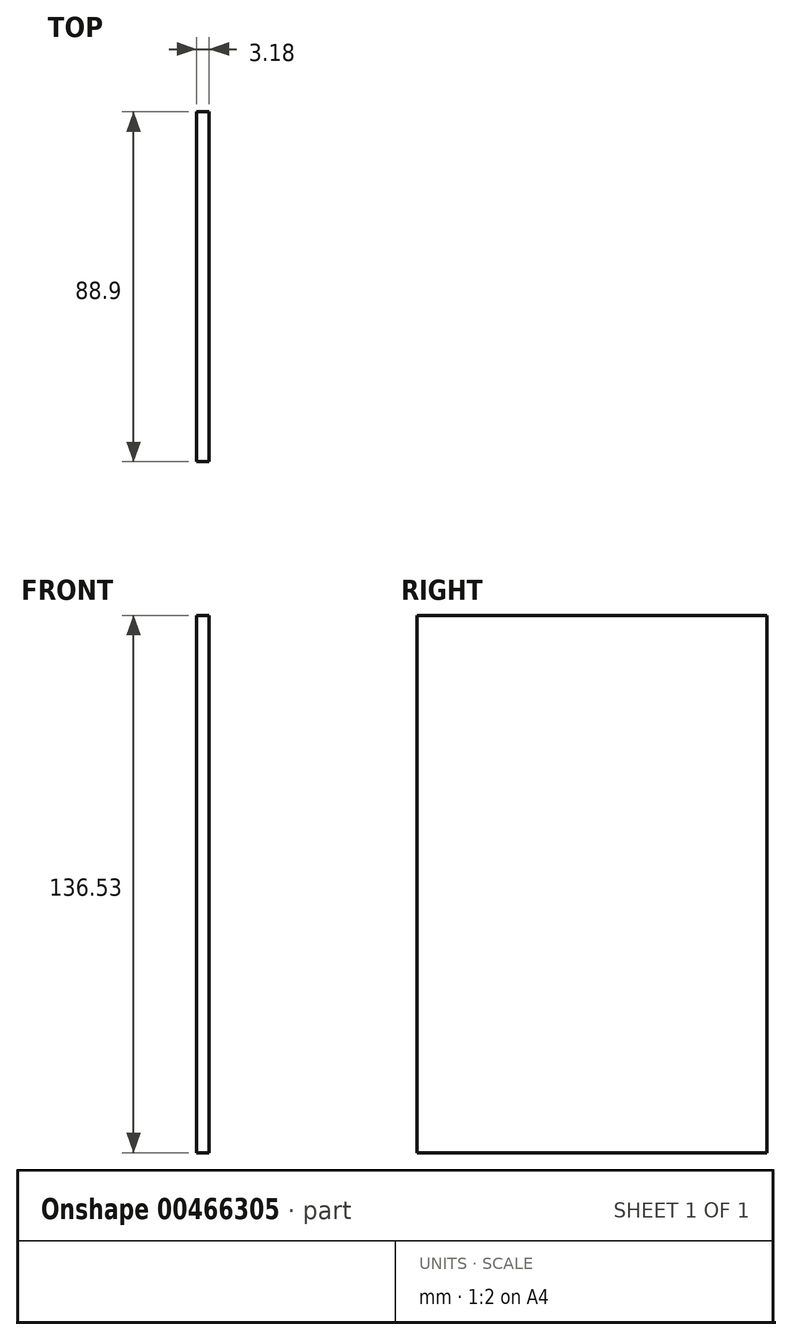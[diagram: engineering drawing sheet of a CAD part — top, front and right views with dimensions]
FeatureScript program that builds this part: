
annotation { "Feature Type Name" : "Feature", "Feature Type Description" : "" }
export const myFeature = defineFeature(function(context is Context, id is Id, definition is map)
    precondition{}
    {
        {
            var Q0;
            Q0=qCreatedBy(makeId("Front.planeOp"),FACE);
            var sketch = newSketch(context, id + "F0", { "sketchPlane" : qUnion([Q0])});
            skLineSegment(sketch, "E0", {"start": v(-45.8, 74.6) * mm, "end": v(-45.8, -61.93) * mm});
            skLineSegment(sketch, "E1", {"start": v(-45.8, -61.93) * mm, "end": v(-48.97, -61.93) * mm});
            skLineSegment(sketch, "E2", {"start": v(-48.97, 74.6) * mm, "end": v(-48.97, -61.93) * mm});
            skLineSegment(sketch, "E3", {"start": v(-45.8, 74.6) * mm, "end": v(-48.97, 74.6) * mm});
            skSolve(sketch);
        }
        {
            var Q0;
            Q0=makeQuery(id+"F0.imprint","IMPRINT",FACE,{"disambiguationData":[TD([[makeQuery(id+"F0.imprint","IMPRINT",EDGE,{"derivedFrom":sQuery(id+"F0.wireOp",EDGE,"E0")}),-1.0]])]});
            extrude(context, id + "F1", {"entities" : qUnion([Q0]), "depth" : 254 * mm});
        }
        {
            var Q0;
            Q0=makeQuery(id+"F1.opExtrude","CAP_FACE",FACE,{"disambiguationData":[OSD([sQuery(id+"F0.wireOp",EDGE,"E0"),sQuery(id+"F0.wireOp",EDGE,"E1"),sQuery(id+"F0.wireOp",EDGE,"E2"),sQuery(id+"F0.wireOp",EDGE,"E3")])],"isStart":false});
            extrude(context, id + "F2", {"entities" : qUnion([Q0]), "operationType" : NewBodyOperationType.REMOVE, "oppositeDirection" : true, "depth" : 165.1 * mm});
        }
    });
